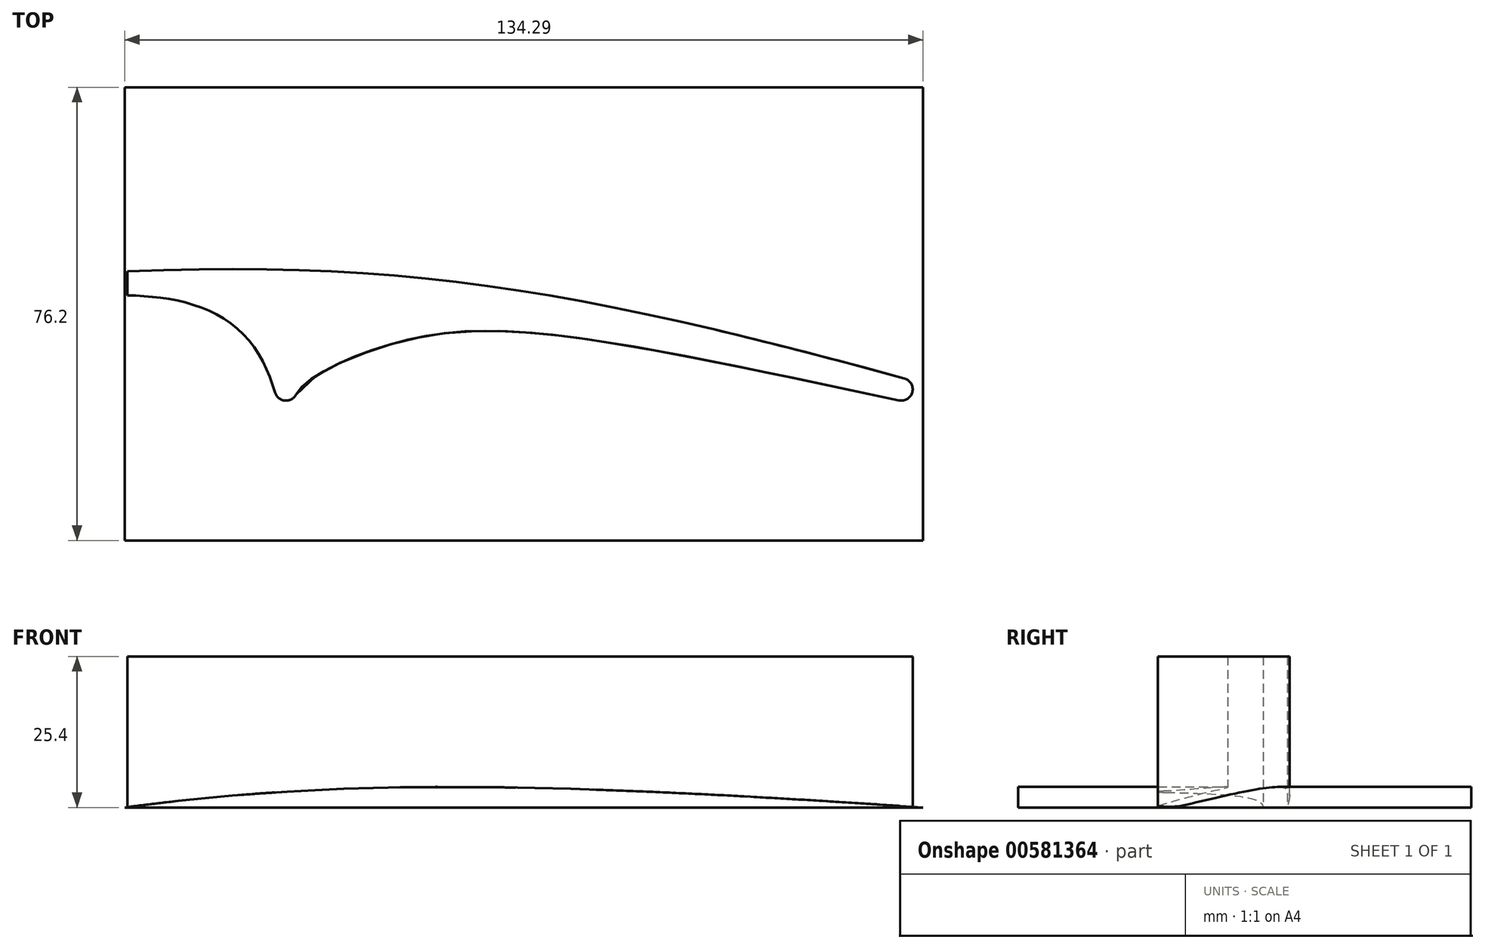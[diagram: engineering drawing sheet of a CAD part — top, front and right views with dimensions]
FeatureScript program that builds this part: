
annotation { "Feature Type Name" : "Feature", "Feature Type Description" : "" }
export const myFeature = defineFeature(function(context is Context, id is Id, definition is map)
    precondition{}
    {
        {
            var Q0;
            Q0=qCreatedBy(makeId("Top.planeOp"),FACE);
            var sketch = newSketch(context, id + "F0", { "sketchPlane" : qUnion([Q0])});
            skArc(sketch, "E0", {"start": v(-41.17, -0.55) * mm, "mid": v(-39.54, -1.9) * mm, "end": v(-37.67, -0.9) * mm});
            skArc(sketch, "E1", {"start": v(63.73, -1.86) * mm, "mid": v(65.98, -0.45) * mm, "end": v(64.64, 1.84) * mm});
            skFitSpline(sketch, "E2", {"points": [v(-66.02, 19.84) * mm, v(64.64, 1.84) * mm], "startDerivative": vector(142.69, 5.72) * mm, "endDerivative": vector(160.12, -43.7) * mm});
            skFitSpline(sketch, "E3", {"points": [v(-37.67, -0.9) * mm, v(-20.6, 7.88) * mm, v(63.73, -1.86) * mm], "startDerivative": vector(15.99, 29.64) * mm, "endDerivative": vector(237.11, -50.95) * mm});
            skFitSpline(sketch, "E4", {"points": [v(-66.02, 15.8) * mm, v(-41.17, -0.55) * mm], "startDerivative": vector(45.41, -1.08) * mm, "endDerivative": vector(9.64, -31.77) * mm});
            skLineSegment(sketch, "E5", {"start": v(-66.02, 19.84) * mm, "end": v(-66.02, 15.8) * mm});
            skSolve(sketch);
        }
        {
            var Q0;
            Q0=qCreatedBy(makeId("Front.planeOp"),FACE);
            var sketch = newSketch(context, id + "F1", { "sketchPlane" : qUnion([Q0])});
            skFitSpline(sketch, "E6", {"points": [v(-66.5, 0) * mm, v(67.8, 0) * mm], "startDerivative": vector(104.67, 13.77) * mm, "endDerivative": vector(203.39, -13.77) * mm});
            skLineSegment(sketch, "E7", {"start": v(67.8, 0) * mm, "end": v(-66.5, 0) * mm});
            skSolve(sketch);
        }
        {
            var Q0;
            Q0 = qSketchRegion(id + "F1", true);
            extrude(context, id + "F2", {"entities" : qUnion([Q0]), "depth" : 25.4 * mm, "offsetDistance" : 25.4 * mm, "hasSecondDirection" : true, "secondDirectionOppositeDirection" : true, "secondDirectionDepth" : 50.8 * mm});
        }
        {
            var Q0;
            Q0=makeQuery(id+"F0.imprint","IMPRINT",FACE,{"disambiguationData":[TD([[makeQuery(id+"F0.imprint","IMPRINT",EDGE,{"derivedFrom":sQuery(id+"F0.wireOp",EDGE,"E0")}),1.0]])]});
            extrude(context, id + "F3", {"entities" : qUnion([Q0]), "operationType" : NewBodyOperationType.ADD, "depth" : 25.4 * mm, "offsetDistance" : 25.4 * mm});
        }
    });
